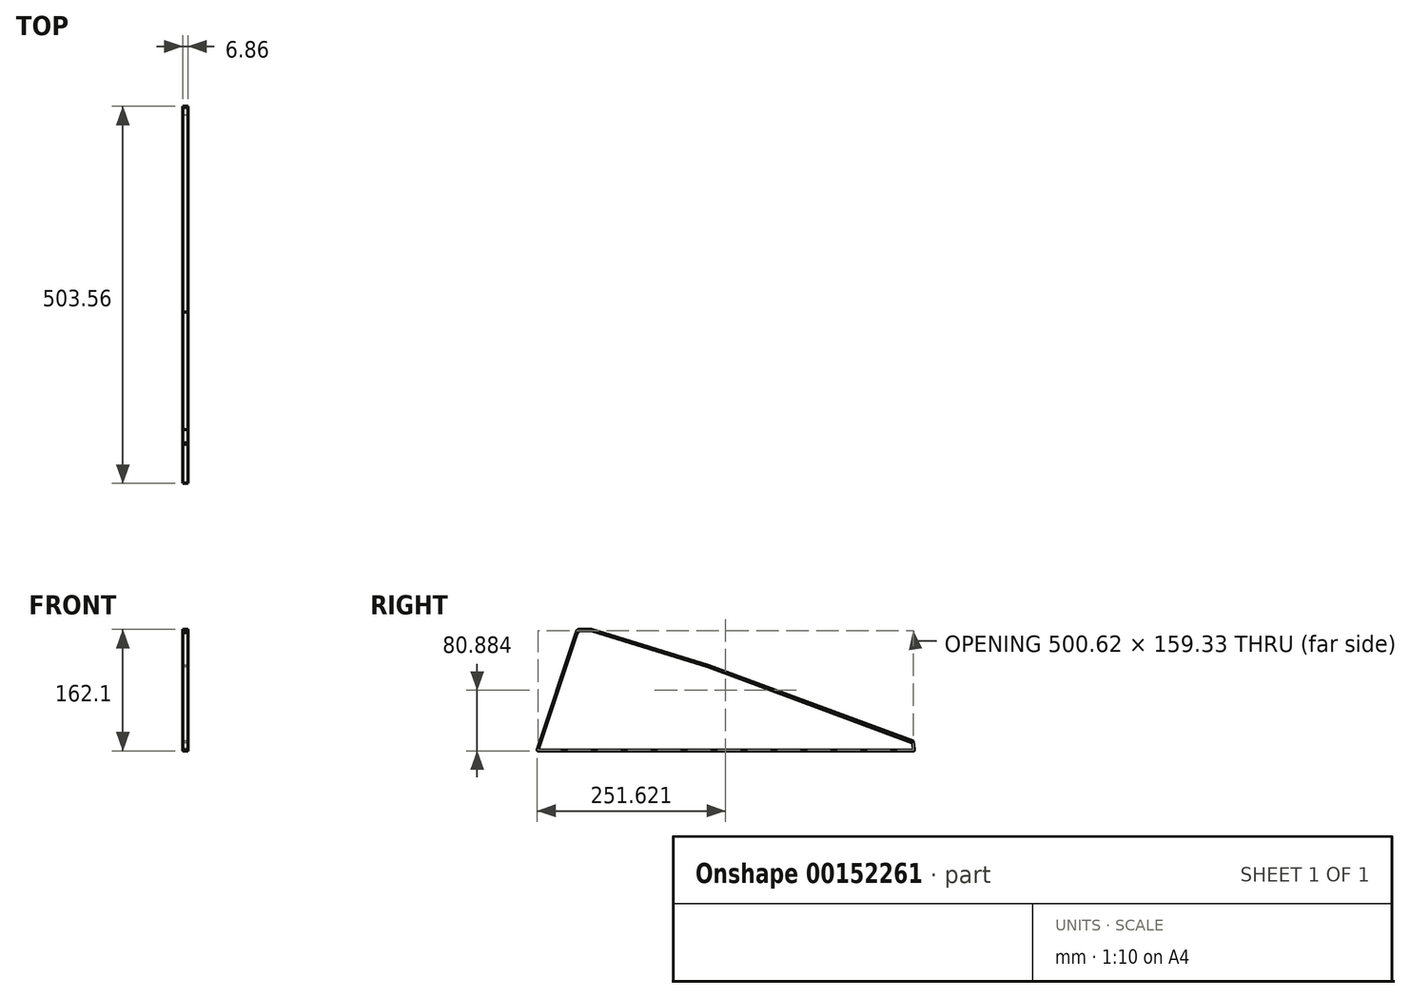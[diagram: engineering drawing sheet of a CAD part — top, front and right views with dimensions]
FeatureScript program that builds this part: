
annotation { "Feature Type Name" : "Feature", "Feature Type Description" : "" }
export const myFeature = defineFeature(function(context is Context, id is Id, definition is map)
    precondition{}
    {
        {
            var Q0;
            Q0=qCreatedBy(makeId("Front.planeOp"),FACE);
            var sketch = newSketch(context, id + "F0", { "sketchPlane" : qUnion([Q0])});
            skLineSegment(sketch, "E0", {"start": v(0, 0) * mm, "end": v(0, 1.27) * mm});
            skLineSegment(sketch, "E1", {"start": v(0, 1.27) * mm, "end": v(6.86, 1.27) * mm});
            skLineSegment(sketch, "E2", {"start": v(6.86, 1.27) * mm, "end": v(6.86, 0) * mm});
            skLineSegment(sketch, "E3", {"start": v(6.86, 0) * mm, "end": v(0, 0) * mm});
            skSolve(sketch);
        }
        {
            var Q0;
            Q0 = qSketchRegion(id + "F0", true);
            extrude(context, id + "F1", {"entities" : qUnion([Q0]), "depth" : 490.22 * mm});
        }
        {
            var Q0;
            Q0=makeQuery(id+"F1.opExtrude","SWEPT_FACE",FACE,{"disambiguationData":[OSD([sQuery(id+"F0.wireOp",EDGE,"E2")])]});
            var sketch = newSketch(context, id + "F2", { "sketchPlane" : qUnion([Q0])});
            skLineSegment(sketch, "E4", {"start": v(-490.22, 1.15) * mm, "end": v(-490.22, 1.27) * mm});
            skLineSegment(sketch, "E5", {"start": v(-490.22, 1.15) * mm, "end": v(-491.5, 1.15) * mm});
            skLineSegment(sketch, "E6", {"start": v(-491.5, 1.15) * mm, "end": v(-491.5, 0.76) * mm});
            skLineSegment(sketch, "E7", {"start": v(-490.73, 0) * mm, "end": v(-490.22, 0) * mm});
            skLineSegment(sketch, "E8", {"start": v(-490.22, 0) * mm, "end": v(-490.22, 1.27) * mm});
            skPoint(sketch, "E9.visualSharp", {"position": v(-491.5, 0) * mm});
            skArc(sketch, "E9.filletArc", {"start": v(-491.5, 0.29) * mm, "mid": v(-491.48, 0.22) * mm, "end": v(-491.46, 0.15) * mm});
            skArc(sketch, "E10.filletArc", {"start": v(-491.5, 0.76) * mm, "mid": v(-491.27, 0.22) * mm, "end": v(-490.73, 0) * mm});
            skLineSegment(sketch, "E11", {"start": v(-490.22, 1.15) * mm, "end": v(-438.07, 157.38) * mm});
            skLineSegment(sketch, "E12", {"start": v(-438.07, 157.38) * mm, "end": v(-439.21, 157.76) * mm});
            skLineSegment(sketch, "E13", {"start": v(-439.21, 157.76) * mm, "end": v(-491.5, 1.15) * mm});
            skSolve(sketch);
        }
        {
            var Q0;
            Q0 = qSketchRegion(id + "F2", true);
            extrude(context, id + "F3", {"entities" : qUnion([Q0]), "operationType" : NewBodyOperationType.ADD, "oppositeDirection" : true, "depth" : 6.86 * mm});
        }
        {
            var Q0;
            Q0=makeQuery(id+"F3.boolean.opBoolean","MERGE",FACE,{"derivedFrom":[makeQuery(id+"F1.opExtrude","SWEPT_FACE",FACE,{"disambiguationData":[OSD([sQuery(id+"F0.wireOp",EDGE,"E0")])]}),makeQuery(id+"F3.opExtrude","CAP_FACE",FACE,{"disambiguationData":[OSD([sQuery(id+"F2.wireOp",EDGE,"E4"),sQuery(id+"F2.wireOp",EDGE,"E5"),sQuery(id+"F2.wireOp",EDGE,"E6"),sQuery(id+"F2.wireOp",EDGE,"E7"),sQuery(id+"F2.wireOp",EDGE,"E8"),sQuery(id+"F2.wireOp",EDGE,"E10.filletArc")])],"isStart":false})]});
            var sketch = newSketch(context, id + "F4", { "sketchPlane" : qUnion([Q0])});
            skLineSegment(sketch, "E14", {"start": v(0, 0) * mm, "end": v(-10.44, 0) * mm});
            skLineSegment(sketch, "E15", {"start": v(-10.44, 0) * mm, "end": v(-10.44, 1.22) * mm});
            skLineSegment(sketch, "E16", {"start": v(-10.44, 1.22) * mm, "end": v(0, 1.22) * mm});
            skLineSegment(sketch, "E17", {"start": v(0, 1.22) * mm, "end": v(0, 0) * mm});
            skLineSegment(sketch, "E18", {"start": v(-10.44, 1.22) * mm, "end": v(-10.44, 3.15) * mm});
            skLineSegment(sketch, "E19", {"start": v(-10.44, 3.15) * mm, "end": v(-11.86, 3.15) * mm});
            skLineSegment(sketch, "E20", {"start": v(-11.85, 0) * mm, "end": v(-10.44, 0) * mm});
            skLineSegment(sketch, "E21", {"start": v(-9.32, 12.3) * mm, "end": v(-10.44, 3.15) * mm});
            skLineSegment(sketch, "E22", {"start": v(-11.86, 3.15) * mm, "end": v(-10.75, 12.86) * mm});
            skLineSegment(sketch, "E23", {"start": v(-10.75, 12.86) * mm, "end": v(-9.24, 12.24) * mm});
            skLineSegment(sketch, "E24", {"start": v(-11.86, 3.15) * mm, "end": v(-12.07, 0.24) * mm});
            skPoint(sketch, "E25.visualSharp", {"position": v(-12.1, 0) * mm});
            skArc(sketch, "E25.filletArc", {"start": v(-12.07, 0.24) * mm, "mid": v(-12.01, 0.07) * mm, "end": v(-11.85, 0) * mm});
            skSolve(sketch);
        }
        {
            var Q0;
            Q0 = qSketchRegion(id + "F4", true);
            extrude(context, id + "F5", {"entities" : qUnion([Q0]), "operationType" : NewBodyOperationType.ADD, "oppositeDirection" : true, "depth" : 6.86 * mm});
        }
        {
            var Q0;
            Q0=makeQuery(id+"F1.opExtrude","CAP_EDGE",EDGE,{"disambiguationData":[OSD([sQuery(id+"F0.wireOp",EDGE,"E1")])],"isStart":true});
            fillet(context, id + "F6", {"entities" : qUnion([Q0]), "radius" : 0.25 * mm, "tangentPropagation" : true, "allowEdgeOverflow" : false});
        }
        {
            var Q0;
            Q0=makeQuery(id+"F5.boolean.opBoolean","MERGE",FACE,{"derivedFrom":[makeQuery(id+"F3.boolean.opBoolean","MERGE",FACE,{"derivedFrom":[makeQuery(id+"F1.opExtrude","SWEPT_FACE",FACE,{"disambiguationData":[OSD([sQuery(id+"F0.wireOp",EDGE,"E2")])]}),makeQuery(id+"F3.opExtrude","CAP_FACE",FACE,{"disambiguationData":[OSD([sQuery(id+"F2.wireOp",EDGE,"E6"),sQuery(id+"F2.wireOp",EDGE,"E7"),sQuery(id+"F2.wireOp",EDGE,"E8"),sQuery(id+"F2.wireOp",EDGE,"E10.filletArc"),sQuery(id+"F2.wireOp",EDGE,"E11"),sQuery(id+"F2.wireOp",EDGE,"E12"),sQuery(id+"F2.wireOp",EDGE,"E13")])],"isStart":true})]}),makeQuery(id+"F5.opExtrude","CAP_FACE",FACE,{"disambiguationData":[OSD([sQuery(id+"F4.wireOp",EDGE,"OOK3ynaC-5ke4-c4XN-tqcq-3eLOP0hLdfmm"),sQuery(id+"F4.wireOp",EDGE,"qEbjVp4W-y8JY-eh2b-dapT-sgq4D78lBT9A"),sQuery(id+"F4.wireOp",EDGE,"sOdCA6Vb-NyWa-rfq0-7aPQ-zu8LECcYTtuX"),sQuery(id+"F4.wireOp",EDGE,"wIzQHS1S-GJdI-iRdi-cc7T-plG9gMv5C61f"),sQuery(id+"F4.wireOp",EDGE,"4255ed0f-ede3-44ff-90f9-e80e1ea1fa6f.filletArc")])],"isStart":false})]});
            var sketch = newSketch(context, id + "F7", { "sketchPlane" : qUnion([Q0])});
            skLineSegment(sketch, "E26", {"start": v(-438.07, 157.38) * mm, "end": v(-439.21, 157.76) * mm});
            skLineSegment(sketch, "E27", {"start": v(-439.21, 157.76) * mm, "end": v(-437.55, 160.9) * mm});
            skLineSegment(sketch, "E28", {"start": v(-437.24, 161) * mm, "end": v(-436.4, 160.55) * mm});
            skLineSegment(sketch, "E29", {"start": v(-436.4, 160.55) * mm, "end": v(-438.07, 157.38) * mm});
            skPoint(sketch, "E30.visualSharp", {"position": v(-437.44, 161.1) * mm});
            skArc(sketch, "E30.filletArc", {"start": v(-437.24, 161) * mm, "mid": v(-437.42, 161.01) * mm, "end": v(-437.55, 160.9) * mm});
            skLineSegment(sketch, "E31", {"start": v(-436.4, 160.55) * mm, "end": v(-419.24, 160.55) * mm});
            skLineSegment(sketch, "E32", {"start": v(-419.24, 160.55) * mm, "end": v(-419.24, 162.1) * mm});
            skLineSegment(sketch, "E33", {"start": v(-419.24, 162.1) * mm, "end": v(-437.02, 162.1) * mm});
            skLineSegment(sketch, "E34", {"start": v(-437.24, 161.87) * mm, "end": v(-437.24, 161) * mm});
            skPoint(sketch, "E35.visualSharp", {"position": v(-437.24, 162.1) * mm});
            skArc(sketch, "E35.filletArc", {"start": v(-437.02, 162.1) * mm, "mid": v(-437.18, 162.03) * mm, "end": v(-437.24, 161.87) * mm});
            skSolve(sketch);
        }
        {
            var Q0;
            Q0 = qSketchRegion(id + "F7", true);
            extrude(context, id + "F8", {"entities" : qUnion([Q0]), "operationType" : NewBodyOperationType.ADD, "oppositeDirection" : true, "depth" : 6.86 * mm});
        }
        {
            var Q0;
            Q0=qCreatedBy(makeId("Right.planeOp"),FACE);
            var sketch = newSketch(context, id + "F9", { "sketchPlane" : qUnion([Q0])});
            skLineSegment(sketch, "E36", {"start": v(9.38, 10.9) * mm, "end": v(-262.9, 111.9) * mm});
            skLineSegment(sketch, "E37", {"start": v(10.71, 12.84) * mm, "end": v(9.38, 10.9) * mm});
            skPoint(sketch, "E38.visualSharp", {"position": v(10.88, 13.08) * mm});
            skArc(sketch, "E38.filletArc", {"start": v(10.71, 12.84) * mm, "mid": v(10.74, 13.04) * mm, "end": v(10.6, 13.18) * mm});
            skLineSegment(sketch, "E39", {"start": v(-262.9, 114) * mm, "end": v(-419.24, 162.1) * mm});
            skLineSegment(sketch, "E40", {"start": v(-419.23, 160.55) * mm, "end": v(-262.9, 111.9) * mm});
            skLineSegment(sketch, "E41", {"start": v(-262.9, 111.9) * mm, "end": v(-262.9, 114) * mm});
            skLineSegment(sketch, "E42.trimOffspring", {"start": v(-262.9, 114) * mm, "end": v(10.6, 13.18) * mm});
            skLineSegment(sketch, "E43", {"start": v(-419.24, 162.1) * mm, "end": v(-419.23, 160.55) * mm});
            skSolve(sketch);
        }
        {
            var Q0;
            Q0 = qSketchRegion(id + "F9", true);
            extrude(context, id + "F10", {"entities" : qUnion([Q0]), "operationType" : NewBodyOperationType.ADD, "depth" : 6.86 * mm});
        }
    });
